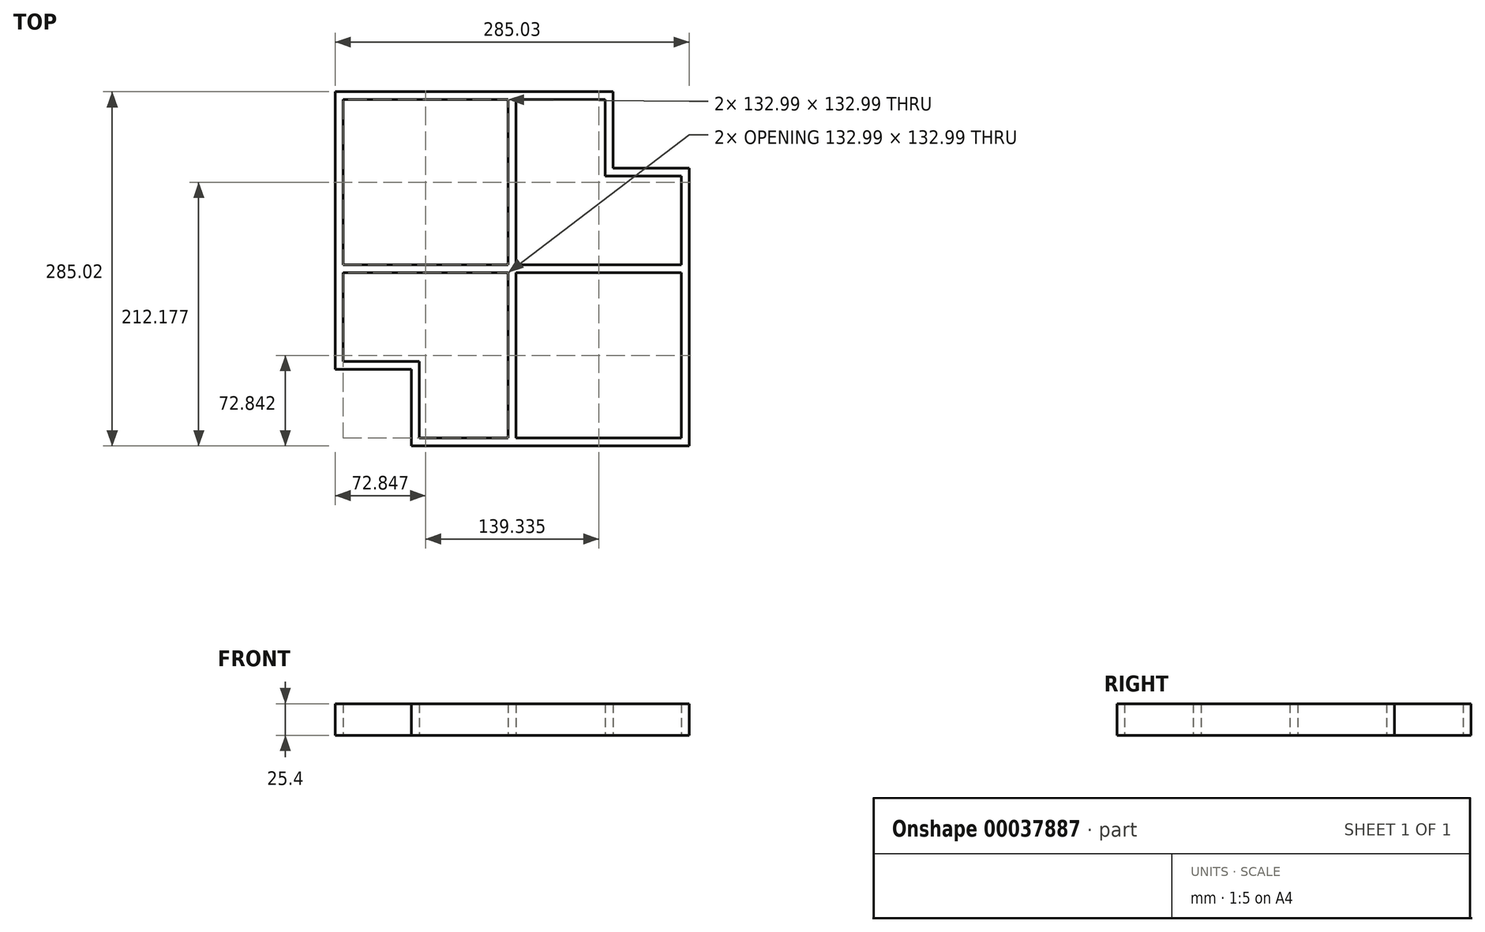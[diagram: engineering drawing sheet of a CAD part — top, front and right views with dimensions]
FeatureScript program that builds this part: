
annotation { "Feature Type Name" : "Feature", "Feature Type Description" : "" }
export const myFeature = defineFeature(function(context is Context, id is Id, definition is map)
    precondition{}
    {
        {
            var Q0;
            Q0=qCreatedBy(makeId("Top.planeOp"),FACE);
            var sketch = newSketch(context, id + "F0", { "sketchPlane" : qUnion([Q0])});
            skLineSegment(sketch, "E0", {"start": v(6.35, 0) * mm, "end": v(77.83, 0) * mm});
            skLineSegment(sketch, "E1", {"start": v(6.35, -139.34) * mm, "end": v(139.34, -139.34) * mm});
            skLineSegment(sketch, "E2", {"start": v(-132.99, -132.99) * mm, "end": v(0, -132.99) * mm});
            skLineSegment(sketch, "E3", {"start": v(-132.99, -132.99) * mm, "end": v(-132.99, 0) * mm});
            skLineSegment(sketch, "E4", {"start": v(6.35, -132.99) * mm, "end": v(139.34, -132.99) * mm});
            skLineSegment(sketch, "E5", {"start": v(6.35, -132.99) * mm, "end": v(6.35, 0) * mm});
            skLineSegment(sketch, "E6", {"start": v(-71.48, -272.32) * mm, "end": v(0, -272.32) * mm});
            skLineSegment(sketch, "E7", {"start": v(0, -132.99) * mm, "end": v(0, 0) * mm});
            skLineSegment(sketch, "E8", {"start": v(-132.99, -210.82) * mm, "end": v(-132.99, -139.34) * mm});
            skLineSegment(sketch, "E9", {"start": v(-132.99, -139.34) * mm, "end": v(0, -139.34) * mm});
            skLineSegment(sketch, "E10", {"start": v(0, -139.34) * mm, "end": v(0, -272.32) * mm});
            skLineSegment(sketch, "E11.bottom", {"start": v(84.18, 6.35) * mm, "end": v(-139.34, 6.35) * mm});
            skLineSegment(sketch, "E11.top", {"start": v(0, 0) * mm, "end": v(-132.99, 0) * mm});
            skLineSegment(sketch, "E12.left", {"start": v(-139.34, -217.17) * mm, "end": v(-139.34, 6.35) * mm});
            skLineSegment(sketch, "E13.bottom", {"start": v(145.69, -278.67) * mm, "end": v(-77.83, -278.67) * mm});
            skLineSegment(sketch, "E13.top", {"start": v(139.34, -272.32) * mm, "end": v(6.35, -272.32) * mm});
            skLineSegment(sketch, "E14.left", {"start": v(139.34, -272.32) * mm, "end": v(139.34, -139.34) * mm});
            skLineSegment(sketch, "E14.right", {"start": v(145.69, -278.67) * mm, "end": v(145.69, -55.15) * mm});
            skLineSegment(sketch, "E15", {"start": v(139.34, -132.99) * mm, "end": v(139.34, -61.5) * mm});
            skLineSegment(sketch, "E16", {"start": v(6.35, -272.32) * mm, "end": v(6.35, -139.34) * mm});
            skLineSegment(sketch, "E17", {"start": v(139.34, -61.5) * mm, "end": v(145.69, -61.5) * mm, "construction": true});
            skLineSegment(sketch, "E18", {"start": v(145.69, -55.15) * mm, "end": v(84.18, -55.15) * mm});
            skLineSegment(sketch, "E19", {"start": v(-132.99, -210.82) * mm, "end": v(-139.34, -210.82) * mm, "construction": true});
            skLineSegment(sketch, "E20", {"start": v(84.18, -55.15) * mm, "end": v(84.18, 6.35) * mm});
            skLineSegment(sketch, "E21", {"start": v(-71.48, -272.32) * mm, "end": v(-71.48, -278.67) * mm, "construction": true});
            skLineSegment(sketch, "E22", {"start": v(139.34, -61.5) * mm, "end": v(77.83, -61.5) * mm});
            skLineSegment(sketch, "E23", {"start": v(0, -272.32) * mm, "end": v(6.35, -272.32) * mm, "construction": true});
            skLineSegment(sketch, "E24", {"start": v(-77.83, -278.67) * mm, "end": v(-77.83, -217.17) * mm});
            skLineSegment(sketch, "E25", {"start": v(-139.34, -217.17) * mm, "end": v(-77.83, -217.17) * mm});
            skLineSegment(sketch, "E26", {"start": v(-71.48, -272.32) * mm, "end": v(-71.48, -210.82) * mm});
            skLineSegment(sketch, "E27", {"start": v(-71.48, -210.82) * mm, "end": v(-132.99, -210.82) * mm});
            skLineSegment(sketch, "E28", {"start": v(77.83, -61.5) * mm, "end": v(77.83, 0) * mm});
            skLineSegment(sketch, "E29.bottom", {"start": v(0, -139.34) * mm, "end": v(6.35, -139.34) * mm, "construction": true});
            skLineSegment(sketch, "E30", {"start": v(77.83, 0) * mm, "end": v(77.83, 6.35) * mm, "construction": true});
            skLineSegment(sketch, "E29.top", {"start": v(0, -132.99) * mm, "end": v(6.35, -132.99) * mm, "construction": true});
            skLineSegment(sketch, "E29.right", {"start": v(6.35, -139.34) * mm, "end": v(6.35, -132.99) * mm, "construction": true});
            skLineSegment(sketch, "E31", {"start": v(84.18, -55.15) * mm, "end": v(77.83, -55.15) * mm, "construction": true});
            skLineSegment(sketch, "E32", {"start": v(84.18, -55.15) * mm, "end": v(84.18, -61.5) * mm, "construction": true});
            skLineSegment(sketch, "E29.left", {"start": v(0, -139.34) * mm, "end": v(0, -132.99) * mm, "construction": true});
            skLineSegment(sketch, "E33", {"start": v(-77.83, -217.17) * mm, "end": v(-77.83, -210.82) * mm, "construction": true});
            skLineSegment(sketch, "E34", {"start": v(-77.83, -217.17) * mm, "end": v(-71.48, -217.17) * mm, "construction": true});
            skLineSegment(sketch, "E35", {"start": v(-132.99, -139.34) * mm, "end": v(-132.99, -132.99) * mm, "construction": true});
            skSolve(sketch);
        }
        {
            var Q0;
            Q0 = qSketchRegion(id + "F0", true);
            extrude(context, id + "F1", {"entities" : qUnion([Q0]), "depth" : 25.4 * mm});
        }
    });
